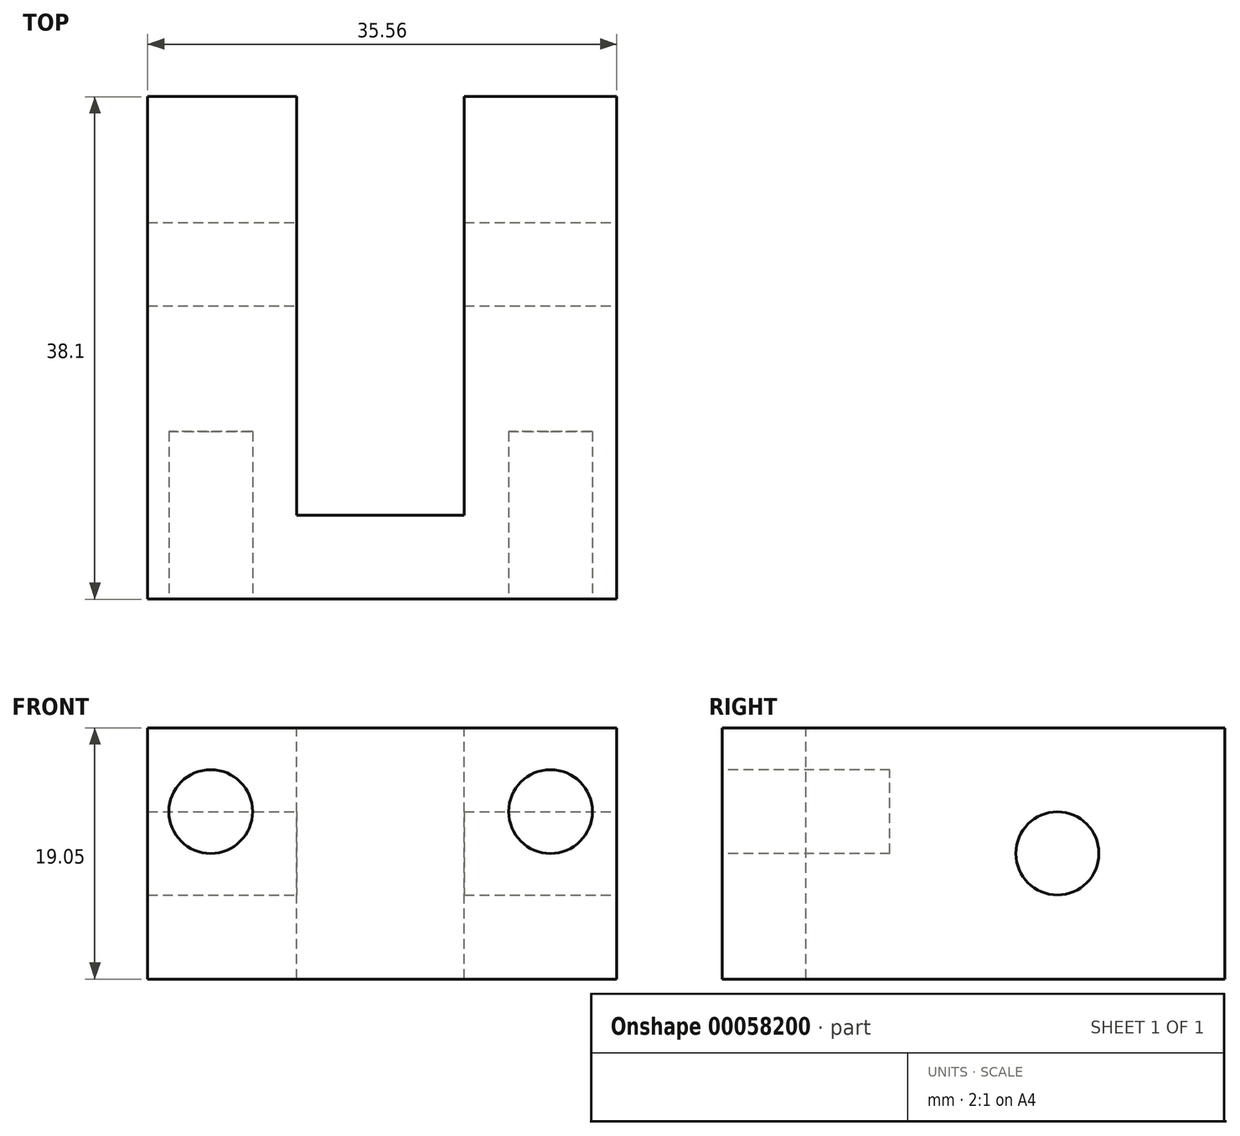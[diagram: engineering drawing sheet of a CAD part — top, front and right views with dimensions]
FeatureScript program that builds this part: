
annotation { "Feature Type Name" : "Feature", "Feature Type Description" : "" }
export const myFeature = defineFeature(function(context is Context, id is Id, definition is map)
    precondition{}
    {
        {
            var Q0;
            Q0=qCreatedBy(makeId("Top.planeOp"),FACE);
            var sketch = newSketch(context, id + "F0", { "sketchPlane" : qUnion([Q0])});
            skLineSegment(sketch, "E0.bottom", {"start": v(-17.66, 20.6) * mm, "end": v(17.9, 20.6) * mm});
            skLineSegment(sketch, "E0.top", {"start": v(-17.66, -17.5) * mm, "end": v(17.9, -17.5) * mm});
            skLineSegment(sketch, "E0.left", {"start": v(-17.66, 20.6) * mm, "end": v(-17.66, -17.5) * mm});
            skLineSegment(sketch, "E0.right", {"start": v(17.9, 20.6) * mm, "end": v(17.9, -17.5) * mm});
            skSolve(sketch);
        }
        {
            var Q0;
            Q0 = qSketchRegion(id + "F0", true);
            extrude(context, id + "F1", {"entities" : qUnion([Q0]), "depth" : 19.05 * mm});
        }
        {
            var Q0;
            Q0=makeQuery(id+"F1.opExtrude","CAP_FACE",FACE,{"disambiguationData":[OSD([sQuery(id+"F0.wireOp",EDGE,"E0.bottom"),sQuery(id+"F0.wireOp",EDGE,"E0.top"),sQuery(id+"F0.wireOp",EDGE,"E0.left"),sQuery(id+"F0.wireOp",EDGE,"E0.right")])],"isStart":false});
            var sketch = newSketch(context, id + "F2", { "sketchPlane" : qUnion([Q0])});
            skLineSegment(sketch, "E1.bottom", {"start": v(-6.35, 20.6) * mm, "end": v(6.35, 20.6) * mm});
            skLineSegment(sketch, "E1.top", {"start": v(-6.35, -11.15) * mm, "end": v(6.35, -11.15) * mm});
            skLineSegment(sketch, "E1.left", {"start": v(-6.35, 20.6) * mm, "end": v(-6.35, -11.15) * mm});
            skLineSegment(sketch, "E1.right", {"start": v(6.35, 20.6) * mm, "end": v(6.35, -11.15) * mm});
            skSolve(sketch);
        }
        {
            var Q0;
            Q0 = qSketchRegion(id + "F2", true);
            extrude(context, id + "F3", {"entities" : qUnion([Q0]), "operationType" : NewBodyOperationType.REMOVE, "oppositeDirection" : true, "depth" : 19.05 * mm});
        }
        {
            var Q0;
            Q0=makeQuery(id+"F1.opExtrude","SWEPT_FACE",FACE,{"disambiguationData":[OSD([sQuery(id+"F0.wireOp",EDGE,"E0.right")])]});
            var sketch = newSketch(context, id + "F4", { "sketchPlane" : qUnion([Q0])});
            skCircle(sketch, "E2", {"center": v(7.9, 9.53) * mm, "radius": 3.15 * mm});
            skSolve(sketch);
        }
        {
            var Q0;
            Q0 = qSketchRegion(id + "F4", true);
            extrude(context, id + "F5", {"entities" : qUnion([Q0]), "operationType" : NewBodyOperationType.REMOVE, "oppositeDirection" : true, "depth" : 35.56 * mm});
        }
        {
            var Q0;
            Q0=makeQuery(id+"F1.opExtrude","SWEPT_FACE",FACE,{"disambiguationData":[OSD([sQuery(id+"F0.wireOp",EDGE,"E0.top")])]});
            var sketch = newSketch(context, id + "F6", { "sketchPlane" : qUnion([Q0])});
            skCircle(sketch, "E3", {"center": v(-12.88, 12.7) * mm, "radius": 3.18 * mm});
            skCircle(sketch, "E4.MirrorC", {"center": v(12.88, 12.7) * mm, "radius": 3.18 * mm});
            skSolve(sketch);
        }
        {
            var Q0;
            Q0 = qSketchRegion(id + "F6", true);
            extrude(context, id + "F7", {"entities" : qUnion([Q0]), "operationType" : NewBodyOperationType.REMOVE, "oppositeDirection" : true, "depth" : 12.7 * mm});
        }
    });
